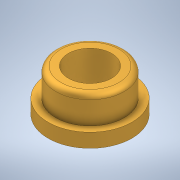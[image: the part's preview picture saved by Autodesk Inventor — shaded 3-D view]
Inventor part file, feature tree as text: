
AUTODESK INVENTOR PART (.ipt)
format: ipt  version: 2022 (Build 260153000, 153)  size: 134,144 bytes
history: native  units: mm
features: extrude x2, sketch x2, fillet x1, projected_geometry x1
ambient origin geometry x8: Origin, YZ Plane, XZ Plane, XY Plane, X Axis, Y Axis, Z Axis, Center Point
bodies: Solid1 (feature_tree)
feature tree (6):
  extrude  "Extrusion1"  Depth=6.2mm
  extrude  "Extrusion2"  Depth=0.75mm
  fillet  "Fillet1"  Radius=2.0mm
  sketch  "Sketch1"  dims[d0=9.8mm d1=6.2mm]
  sketch  "Sketch2"  dims[d2=6.0mm d3=0.0mm d4=12.0mm d5=2.0mm d6=0.0mm d7=0.75mm]
  projected_geometry  "Projected Loop1"
